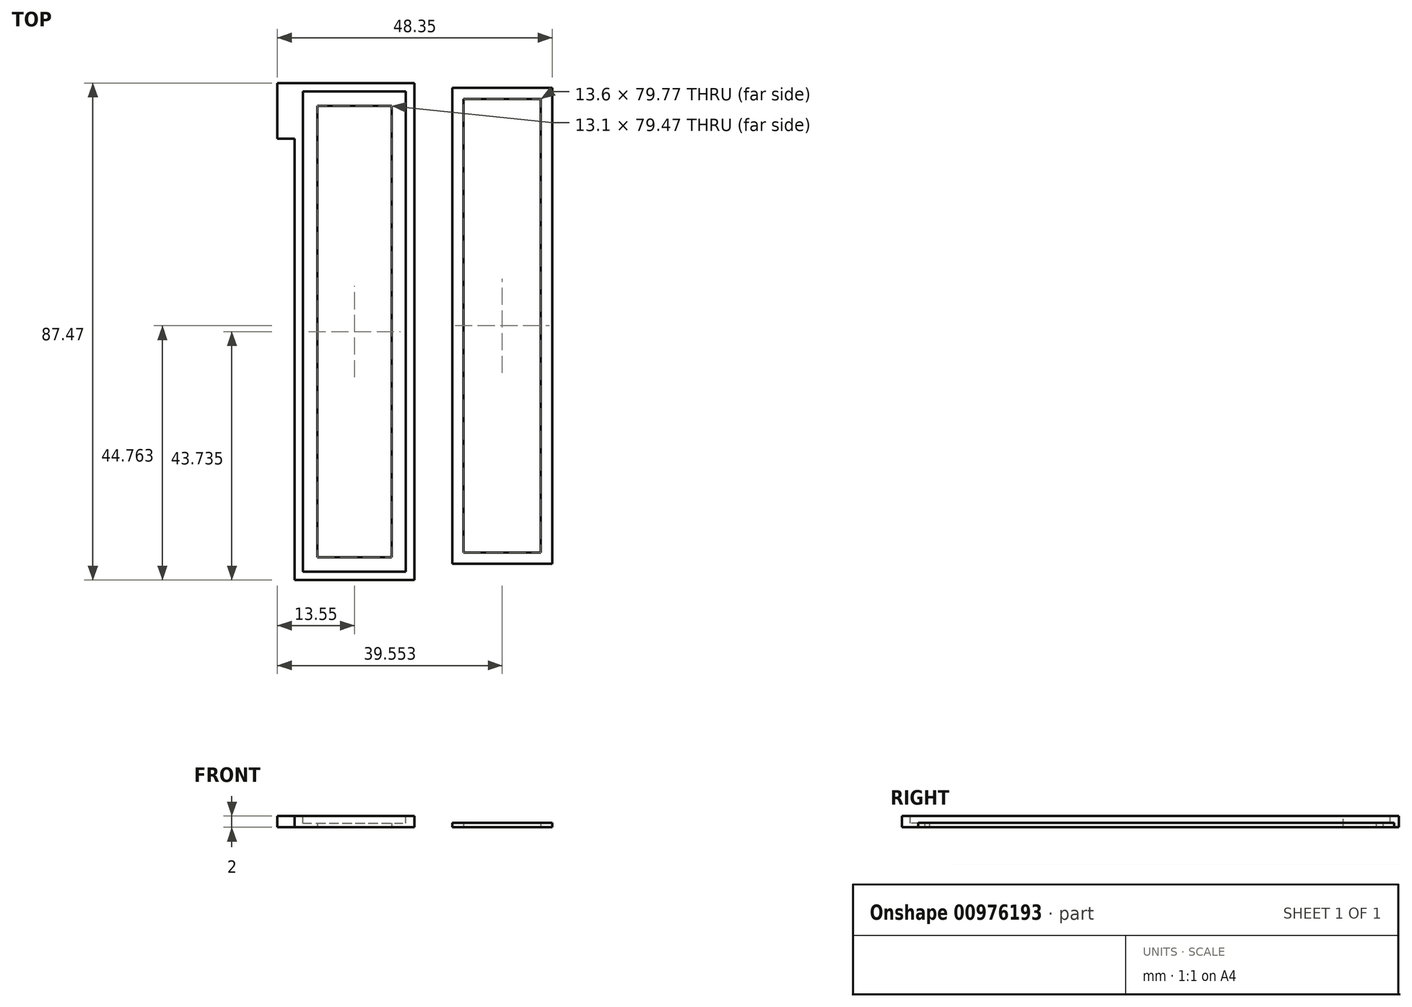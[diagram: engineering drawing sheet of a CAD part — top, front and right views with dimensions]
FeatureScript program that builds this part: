
annotation { "Feature Type Name" : "Feature", "Feature Type Description" : "" }
export const myFeature = defineFeature(function(context is Context, id is Id, definition is map)
    precondition{}
    {
        {
            var Q0;
            Q0=qCreatedBy(makeId("Top.planeOp"),FACE);
            var sketch = newSketch(context, id + "F0", { "sketchPlane" : qUnion([Q0])});
            skLineSegment(sketch, "E0.bottom", {"start": v(0, 0) * mm, "end": v(21.1, 0) * mm});
            skLineSegment(sketch, "E0.top", {"start": v(0, 87.47) * mm, "end": v(21.1, 87.47) * mm});
            skLineSegment(sketch, "E0.left", {"start": v(0, 0) * mm, "end": v(0, 87.47) * mm});
            skLineSegment(sketch, "E0.right", {"start": v(21.1, 0) * mm, "end": v(21.1, 87.47) * mm});
            skLineSegment(sketch, "E1.bottom", {"start": v(4, 83.47) * mm, "end": v(17.1, 83.47) * mm});
            skLineSegment(sketch, "E1.top", {"start": v(4, 4) * mm, "end": v(17.1, 4) * mm});
            skLineSegment(sketch, "E1.left", {"start": v(4, 83.47) * mm, "end": v(4, 4) * mm});
            skLineSegment(sketch, "E1.right", {"start": v(17.1, 83.47) * mm, "end": v(17.1, 4) * mm});
            skSolve(sketch);
        }
        {
            var Q0;
            Q0=qSketchRegion(id+"F0",true);
            extrude(context, id + "F1", {"entities" : qUnion([Q0]), "depth" : 2 * mm, "offsetDistance" : 25 * mm});
        }
        {
            var Q0;
            Q0=makeQuery(id+"F1.opExtrude","CAP_FACE",FACE,{"disambiguationData":[OSD([sQuery(id+"F0.wireOp",EDGE,"E0.bottom"),sQuery(id+"F0.wireOp",EDGE,"E0.top"),sQuery(id+"F0.wireOp",EDGE,"E0.left"),sQuery(id+"F0.wireOp",EDGE,"E0.right"),sQuery(id+"F0.wireOp",EDGE,"E1.bottom"),sQuery(id+"F0.wireOp",EDGE,"E1.top"),sQuery(id+"F0.wireOp",EDGE,"E1.left"),sQuery(id+"F0.wireOp",EDGE,"E1.right")])],"isStart":false});
            var sketch = newSketch(context, id + "F2", { "sketchPlane" : qUnion([Q0])});
            skLineSegment(sketch, "E2.bottom", {"start": v(1.5, 85.97) * mm, "end": v(19.6, 85.97) * mm});
            skLineSegment(sketch, "E2.top", {"start": v(1.5, 1.5) * mm, "end": v(19.6, 1.5) * mm});
            skLineSegment(sketch, "E2.left", {"start": v(1.5, 85.97) * mm, "end": v(1.5, 1.5) * mm});
            skLineSegment(sketch, "E2.right", {"start": v(19.6, 85.97) * mm, "end": v(19.6, 1.5) * mm});
            skSolve(sketch);
        }
        {
            var Q0;
            Q0=qSketchRegion(id+"F2",true);
            extrude(context, id + "F3", {"entities" : qUnion([Q0]), "operationType" : NewBodyOperationType.REMOVE, "oppositeDirection" : true, "depth" : 1.25 * mm, "offsetDistance" : 25 * mm});
        }
        {
            var Q0;
            Q0=qCreatedBy(makeId("Top.planeOp"),FACE);
            var sketch = newSketch(context, id + "F4", { "sketchPlane" : qUnion([Q0])});
            skLineSegment(sketch, "E3.bottom", {"start": v(27.75, 86.65) * mm, "end": v(45.35, 86.65) * mm});
            skLineSegment(sketch, "E3.top", {"start": v(27.75, 2.88) * mm, "end": v(45.35, 2.88) * mm});
            skLineSegment(sketch, "E3.left", {"start": v(27.75, 86.65) * mm, "end": v(27.75, 2.88) * mm});
            skLineSegment(sketch, "E3.right", {"start": v(45.35, 86.65) * mm, "end": v(45.35, 2.88) * mm});
            skLineSegment(sketch, "E4.bottom", {"start": v(29.75, 84.65) * mm, "end": v(43.35, 84.65) * mm});
            skLineSegment(sketch, "E4.top", {"start": v(29.75, 4.88) * mm, "end": v(43.35, 4.88) * mm});
            skLineSegment(sketch, "E4.left", {"start": v(29.75, 84.65) * mm, "end": v(29.75, 4.88) * mm});
            skLineSegment(sketch, "E4.right", {"start": v(43.35, 84.65) * mm, "end": v(43.35, 4.88) * mm});
            skSolve(sketch);
        }
        {
            var Q0;
            Q0=qSketchRegion(id+"F4",true);
            extrude(context, id + "F5", {"entities" : qUnion([Q0]), "depth" : 0.8 * mm, "offsetDistance" : 25 * mm});
        }
        {
            var Q0;
            Q0=makeQuery(id+"F1.opExtrude","SWEPT_FACE",FACE,{"disambiguationData":[OSD([sQuery(id+"F0.wireOp",EDGE,"E0.left")])]});
            var sketch = newSketch(context, id + "F6", { "sketchPlane" : qUnion([Q0])});
            skLineSegment(sketch, "E5.bottom", {"start": v(-87.47, 0) * mm, "end": v(-77.67, 0) * mm});
            skLineSegment(sketch, "E5.top", {"start": v(-87.47, 2) * mm, "end": v(-77.67, 2) * mm});
            skLineSegment(sketch, "E5.left", {"start": v(-87.47, 0) * mm, "end": v(-87.47, 2) * mm});
            skLineSegment(sketch, "E5.right", {"start": v(-77.67, 0) * mm, "end": v(-77.67, 2) * mm});
            skSolve(sketch);
        }
        {
            var Q0;
            Q0=qSketchRegion(id+"F6",true);
            extrude(context, id + "F7", {"entities" : qUnion([Q0]), "operationType" : NewBodyOperationType.ADD, "depth" : 3 * mm, "offsetDistance" : 25 * mm});
        }
    });
